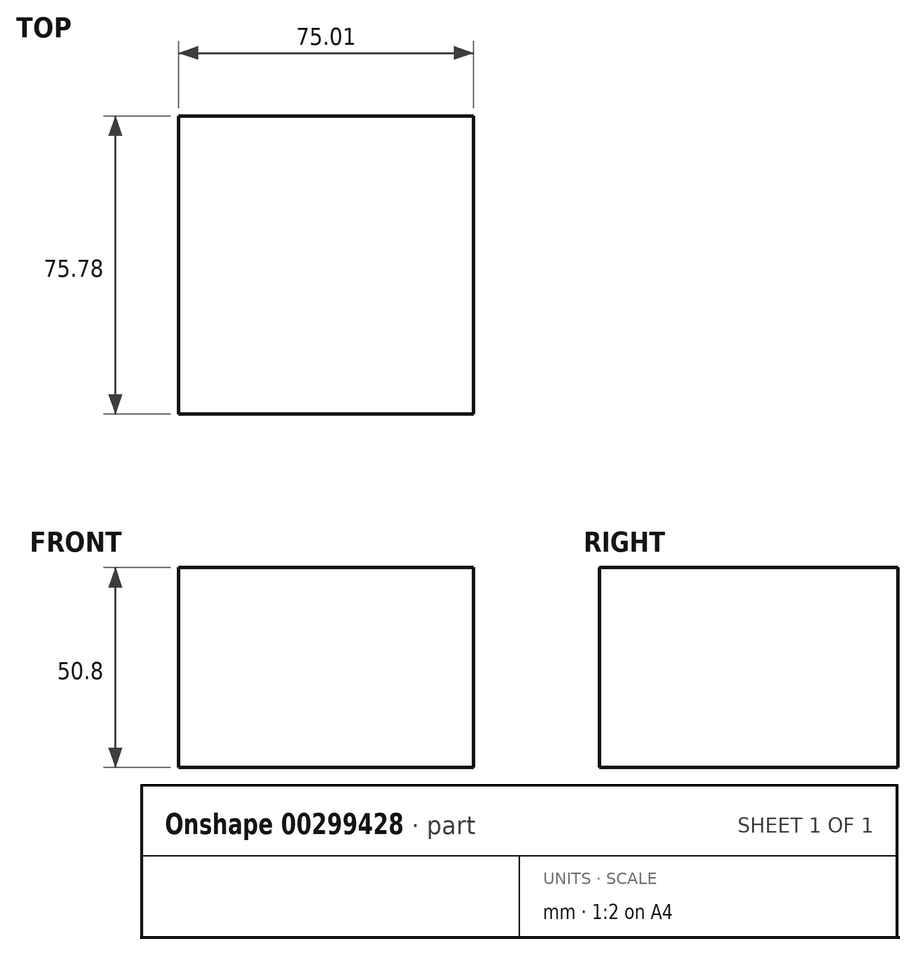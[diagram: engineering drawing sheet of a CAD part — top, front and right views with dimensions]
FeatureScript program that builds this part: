
annotation { "Feature Type Name" : "Feature", "Feature Type Description" : "" }
export const myFeature = defineFeature(function(context is Context, id is Id, definition is map)
    precondition{}
    {
        {
            var Q0;
            Q0=qCreatedBy(makeId("Top.planeOp"),FACE);
            var sketch = newSketch(context, id + "F0", { "sketchPlane" : qUnion([Q0])});
            skLineSegment(sketch, "E0.bottom", {"start": v(0, 0) * mm, "end": v(75.01, 0) * mm});
            skLineSegment(sketch, "E0.top", {"start": v(0, 75.78) * mm, "end": v(75.01, 75.78) * mm});
            skLineSegment(sketch, "E0.left", {"start": v(0, 0) * mm, "end": v(0, 75.78) * mm});
            skLineSegment(sketch, "E0.right", {"start": v(75.01, 0) * mm, "end": v(75.01, 75.78) * mm});
            skSolve(sketch);
        }
        {
            var Q0;
            Q0=qSketchRegion(id+"F0",true);
            extrude(context, id + "F1", {"entities" : qUnion([Q0]), "depth" : 50.8 * mm});
        }
    });
